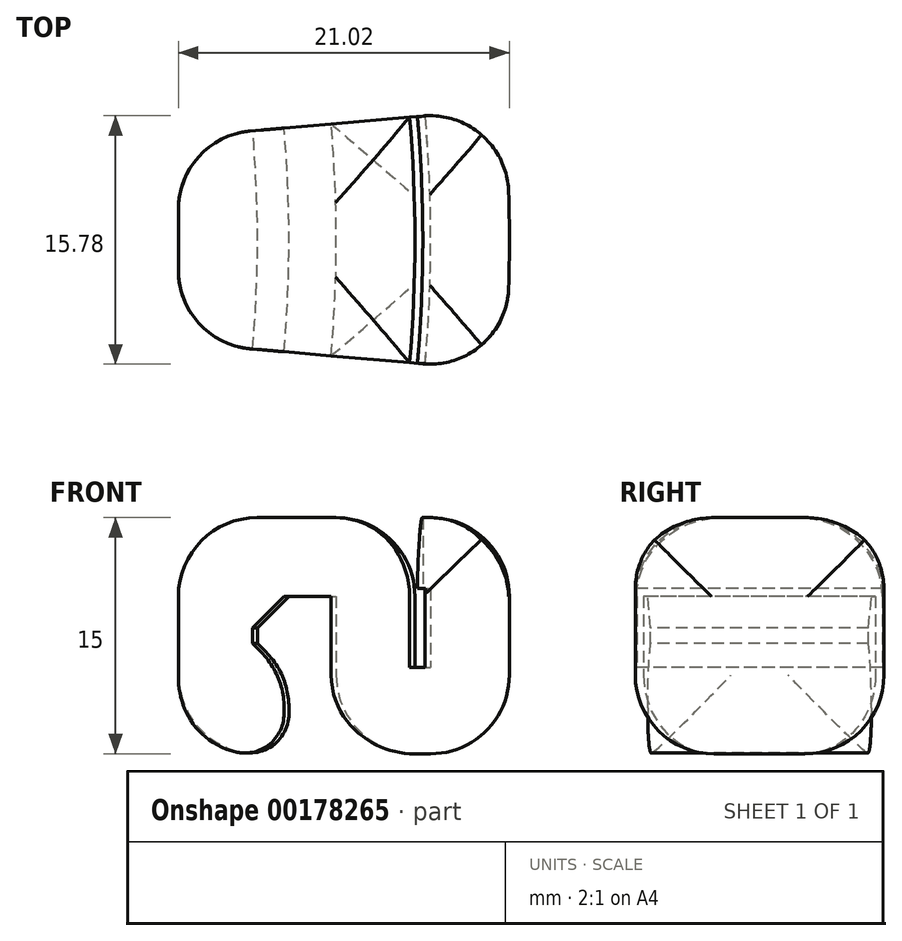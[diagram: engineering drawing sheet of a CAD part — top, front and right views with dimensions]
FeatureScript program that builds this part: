
annotation { "Feature Type Name" : "Feature", "Feature Type Description" : "" }
export const myFeature = defineFeature(function(context is Context, id is Id, definition is map)
    precondition{}
    {
        {
            var Q0;
            Q0=qCreatedBy(makeId("Front.planeOp"),FACE);
            var sketch = newSketch(context, id + "F0", { "sketchPlane" : qUnion([Q0])});
            skLineSegment(sketch, "E0", {"start": v(0, 0) * mm, "end": v(0, 137.78) * mm, "construction": true});
            skLineSegment(sketch, "E1", {"start": v(0, 0) * mm, "end": v(84, 0) * mm, "construction": true});
            skArc(sketch, "E2", {"start": v(20.4, -69.7) * mm, "mid": v(65.7, -47.18) * mm, "end": v(84, 0) * mm, "construction": true});
            skLineSegment(sketch, "E3", {"start": v(84, 0) * mm, "end": v(84, 12) * mm, "construction": true});
            skLineSegment(sketch, "E4", {"start": v(82, 0) * mm, "end": v(82, 16.28) * mm, "construction": true});
            skArc(sketch, "E5", {"start": v(20.4, -67.7) * mm, "mid": v(63.61, -46.5) * mm, "end": v(81.97, -2) * mm, "construction": true});
            skLineSegment(sketch, "E6", {"start": v(20.4, -69.7) * mm, "end": v(20.4, -67.7) * mm, "construction": true});
            skArc(sketch, "E7", {"start": v(81.97, -2) * mm, "mid": v(82, -1) * mm, "end": v(82, 0) * mm, "construction": true});
            skArc(sketch, "E8", {"start": v(81.97, -2) * mm, "mid": v(83.4, -1.42) * mm, "end": v(84, 0) * mm, "construction": true});
            skArc(sketch, "E9", {"start": v(84, 0) * mm, "mid": v(80.6, 1.42) * mm, "end": v(81.97, -2) * mm, "construction": true});
            skLineSegment(sketch, "E10", {"start": v(79.5, -2.5) * mm, "end": v(79.5, 2.5) * mm});
            skLineSegment(sketch, "E11", {"start": v(79.5, 2.5) * mm, "end": v(84.5, 2.5) * mm});
            skLineSegment(sketch, "E12", {"start": v(84.5, 2.5) * mm, "end": v(84.5, -7.5) * mm});
            skLineSegment(sketch, "E13", {"start": v(81.5, -7.5) * mm, "end": v(74.5, -7.5) * mm});
            skLineSegment(sketch, "E14", {"start": v(74.5, -7.5) * mm, "end": v(74.5, 7.5) * mm});
            skLineSegment(sketch, "E15", {"start": v(74.5, 7.5) * mm, "end": v(89.5, 7.5) * mm});
            skLineSegment(sketch, "E16", {"start": v(89.5, 7.5) * mm, "end": v(89.5, -2) * mm});
            skLineSegment(sketch, "E17", {"start": v(89.5, -2) * mm, "end": v(90.5, -2) * mm});
            skLineSegment(sketch, "E18", {"start": v(90, 7.5) * mm, "end": v(95.5, 7.5) * mm});
            skLineSegment(sketch, "E19", {"start": v(95.5, 7.5) * mm, "end": v(95.5, -7.5) * mm});
            skLineSegment(sketch, "E20", {"start": v(95.5, -7.5) * mm, "end": v(84.5, -7.5) * mm});
            skLineSegment(sketch, "E21", {"start": v(90, 3) * mm, "end": v(90.5, 3) * mm});
            skLineSegment(sketch, "E22", {"start": v(90.5, 3) * mm, "end": v(90.5, -2) * mm});
            skLineSegment(sketch, "E23", {"start": v(90, 3) * mm, "end": v(90, 7.5) * mm});
            skLineSegment(sketch, "E24", {"start": v(79.5, -2.5) * mm, "end": v(81.5, -2.5) * mm});
            skLineSegment(sketch, "E25", {"start": v(81.5, -2.5) * mm, "end": v(81.5, -7.5) * mm});
            skSolve(sketch);
        }
        {
            var Q0;
            Q0=makeQuery(id+"F0.imprint","IMPRINT",FACE,{"disambiguationData":[TD([[makeQuery(id+"F0.imprint","IMPRINT",EDGE,{"derivedFrom":sQuery(id+"F0.wireOp",EDGE,"E10")}),1.0]])]});
            var Q1;
            Q1=sQuery(id+"F0.wireOp",EDGE,"E0");
            revolve(context, id + "F1", {"entities" : qUnion([Q0]), "axis" : qUnion([Q1]), "revolveType" : RevolveType.SYMMETRIC, "angle" : 10 * degree});
        }
        {
            var Q0;
            Q0=makeQuery(id+"F1.opRevolve","SWEPT_EDGE",EDGE,{"disambiguationData":[OSD([sQuery(id+"F0.wireOp",EDGE,"E14"),sQuery(id+"F0.wireOp",EDGE,"E15")])]});
            var Q1;
            Q1=makeQuery(id+"F1.opRevolve","SWEPT_EDGE",EDGE,{"disambiguationData":[OSD([sQuery(id+"F0.wireOp",EDGE,"E13"),sQuery(id+"F0.wireOp",EDGE,"E14")])]});
            var Q2;
            Q2=makeQuery(id+"F1.opRevolve","SWEPT_EDGE",EDGE,{"disambiguationData":[OSD([sQuery(id+"F0.wireOp",EDGE,"E19"),sQuery(id+"F0.wireOp",EDGE,"E20")])]});
            var Q3;
            Q3=makeQuery(id+"F1.opRevolve","SWEPT_EDGE",EDGE,{"disambiguationData":[OSD([sQuery(id+"F0.wireOp",EDGE,"E18"),sQuery(id+"F0.wireOp",EDGE,"E19")])]});
            var Q4;
            Q4=makeQuery(id+"F1.opRevolve","SWEPT_EDGE",EDGE,{"disambiguationData":[OSD([sQuery(id+"F0.wireOp",EDGE,"E15"),sQuery(id+"F0.wireOp",EDGE,"E16")])]});
            fillet(context, id + "F2", {"entities" : qUnion([Q0, Q1, Q2, Q3, Q4]), "radius" : 5 * mm, "tangentPropagation" : true, "allowEdgeOverflow" : false});
        }
        {
            var Q0;
            Q0=makeQuery(id+"F1.opRevolve","SWEPT_EDGE",EDGE,{"disambiguationData":[OSD([sQuery(id+"F0.wireOp",EDGE,"E10"),sQuery(id+"F0.wireOp",EDGE,"E11")])]});
            var Q1;
            Q1=makeQuery(id+"F1.opRevolve","SWEPT_EDGE",EDGE,{"disambiguationData":[OSD([sQuery(id+"F0.wireOp",EDGE,"E10"),sQuery(id+"F0.wireOp",EDGE,"E24")])]});
            chamfer(context, id + "F3", {"entities" : qUnion([Q0, Q1]), "width" : 2 * mm, "tangentPropagation" : true});
        }
        {
            var Q0;
            Q0=makeQuery(id+"F1.opRevolve","SWEPT_EDGE",EDGE,{"disambiguationData":[OSD([sQuery(id+"F0.wireOp",EDGE,"E13"),sQuery(id+"F0.wireOp",EDGE,"E25")])]});
            fillet(context, id + "F4", {"entities" : qUnion([Q0]), "radius" : 2.5 * mm, "tangentPropagation" : true, "allowEdgeOverflow" : false});
        }
        {
            var Q0;
            Q0=makeQuery(id+"F3.opChamfer","BLEND_EDGE",EDGE,{"blendedFrom":[makeQuery(id+"F1.opRevolve","SWEPT_EDGE",EDGE,{"disambiguationData":[OSD([sQuery(id+"F0.wireOp",EDGE,"E10"),sQuery(id+"F0.wireOp",EDGE,"E24")])]}),makeQuery(id+"F1.opRevolve","SWEPT_FACE",FACE,{"disambiguationData":[OSD([sQuery(id+"F0.wireOp",EDGE,"E25")])]})],"blendedInto":[makeQuery(id+"F1.opRevolve","SWEPT_FACE",FACE,{"disambiguationData":[OSD([sQuery(id+"F0.wireOp",EDGE,"E25")])]})]});
            var Q1;
            {var subQ0=sQuery(id+"F0.wireOp",EDGE,"E12");Q1=makeQuery(id+"F3.opChamfer","BLEND_EDGE",EDGE,{"blendedFrom":[makeQuery(id+"F1.opRevolve","SWEPT_EDGE",EDGE,{"disambiguationData":[OSD([subQ0,sQuery(id+"F0.wireOp",EDGE,"E20")])]}),makeQuery(id+"F1.opRevolve","SWEPT_FACE",FACE,{"disambiguationData":[OSD([subQ0])]})],"blendedInto":[makeQuery(id+"F1.opRevolve","SWEPT_FACE",FACE,{"disambiguationData":[OSD([subQ0])]})]});}
            var Q2;
            Q2=makeQuery(id+"F1.opRevolve","SWEPT_EDGE",EDGE,{"disambiguationData":[OSD([sQuery(id+"F0.wireOp",EDGE,"E12"),sQuery(id+"F0.wireOp",EDGE,"E20")])]});
            fillet(context, id + "F5", {"entities" : qUnion([Q0, Q1, Q2]), "radius" : 5 * mm, "tangentPropagation" : true, "allowEdgeOverflow" : false});
        }
        {
            var Q0;
            Q0=makeQuery(id+"F1.opRevolve","CAP_EDGE",EDGE,{"disambiguationData":[OSD([sQuery(id+"F0.wireOp",EDGE,"E15")])],"isStart":true});
            var Q1;
            Q1=makeQuery(id+"F1.opRevolve","CAP_EDGE",EDGE,{"disambiguationData":[OSD([sQuery(id+"F0.wireOp",EDGE,"E15")])],"isStart":false});
            var Q2;
            Q2=makeQuery(id+"F1.opRevolve","CAP_EDGE",EDGE,{"disambiguationData":[OSD([sQuery(id+"F0.wireOp",EDGE,"E18")])],"isStart":true});
            var Q3;
            Q3=makeQuery(id+"F1.opRevolve","CAP_EDGE",EDGE,{"disambiguationData":[OSD([sQuery(id+"F0.wireOp",EDGE,"E18")])],"isStart":false});
            var Q4;
            Q4=makeQuery(id+"F1.opRevolve","CAP_EDGE",EDGE,{"disambiguationData":[OSD([sQuery(id+"F0.wireOp",EDGE,"E19")])],"isStart":true});
            var Q5;
            Q5=makeQuery(id+"F1.opRevolve","CAP_EDGE",EDGE,{"disambiguationData":[OSD([sQuery(id+"F0.wireOp",EDGE,"E19")])],"isStart":false});
            var Q6;
            Q6=makeQuery(id+"F1.opRevolve","CAP_EDGE",EDGE,{"disambiguationData":[OSD([sQuery(id+"F0.wireOp",EDGE,"E20")])],"isStart":true});
            var Q7;
            Q7=makeQuery(id+"F1.opRevolve","CAP_EDGE",EDGE,{"disambiguationData":[OSD([sQuery(id+"F0.wireOp",EDGE,"E20")])],"isStart":false});
            var Q8;
            Q8=makeQuery(id+"F1.opRevolve","CAP_EDGE",EDGE,{"disambiguationData":[OSD([sQuery(id+"F0.wireOp",EDGE,"E14")])],"isStart":true});
            var Q9;
            Q9=makeQuery(id+"F1.opRevolve","CAP_EDGE",EDGE,{"disambiguationData":[OSD([sQuery(id+"F0.wireOp",EDGE,"E14")])],"isStart":false});
            fillet(context, id + "F6", {"entities" : qUnion([Q0, Q1, Q2, Q3, Q4, Q5, Q6, Q7, Q8, Q9]), "radius" : 5 * mm, "allowEdgeOverflow" : false});
        }
    });
